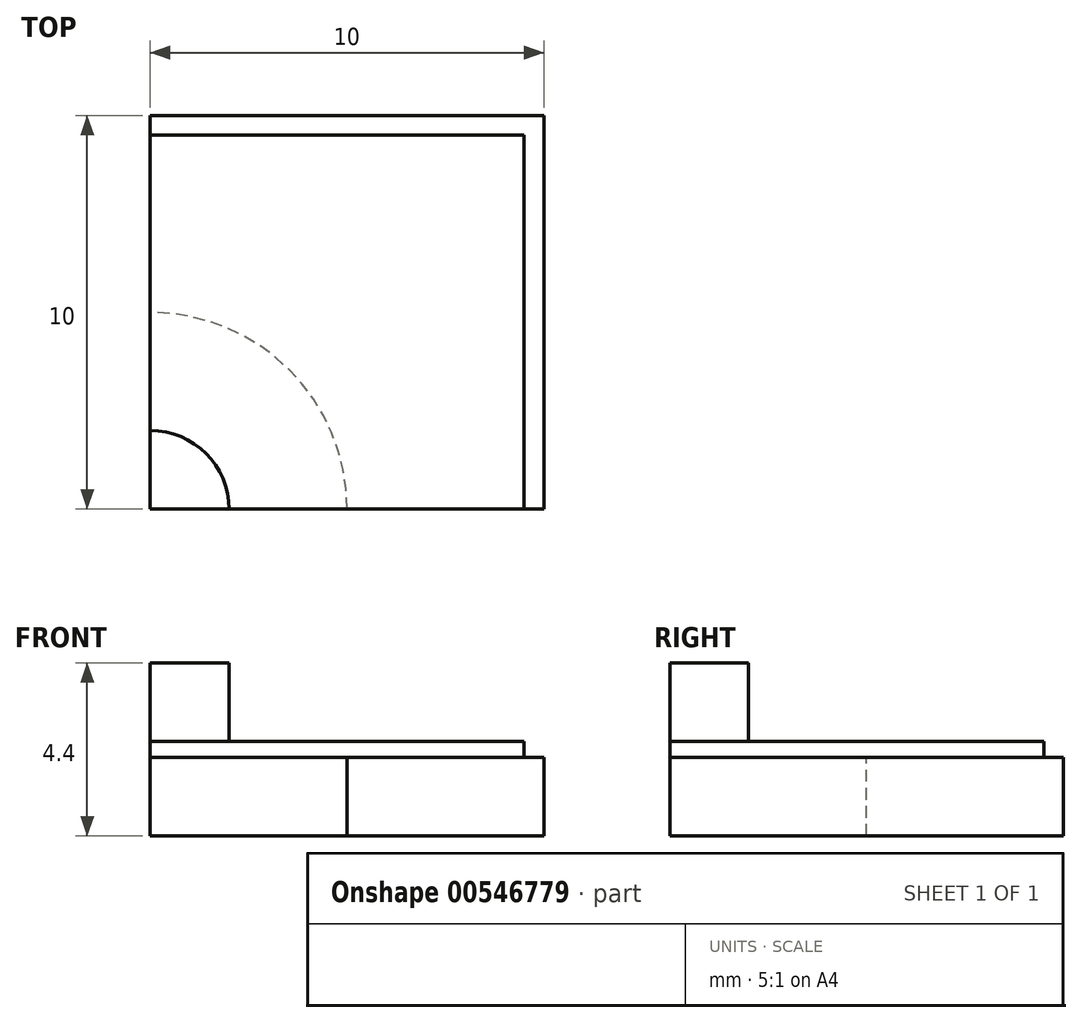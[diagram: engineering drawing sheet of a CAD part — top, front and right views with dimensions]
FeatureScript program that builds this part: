
annotation { "Feature Type Name" : "Feature", "Feature Type Description" : "" }
export const myFeature = defineFeature(function(context is Context, id is Id, definition is map)
    precondition{}
    {
        {
            var Q0;
            Q0=qCreatedBy(makeId("Top.planeOp"),FACE);
            var sketch = newSketch(context, id + "F0", { "sketchPlane" : qUnion([Q0])});
            skLineSegment(sketch, "E0.bottom", {"start": v(0, 0) * mm, "end": v(10, 0) * mm, "construction": true});
            skLineSegment(sketch, "E0.top", {"start": v(0, 10) * mm, "end": v(10, 10) * mm, "construction": true});
            skLineSegment(sketch, "E0.left", {"start": v(0, 0) * mm, "end": v(0, 10) * mm, "construction": true});
            skLineSegment(sketch, "E0.right", {"start": v(10, 0) * mm, "end": v(10, 10) * mm, "construction": true});
            skCircle(sketch, "E1", {"center": v(0, 0) * mm, "radius": 5 * mm, "construction": true});
            skArc(sketch, "E2", {"start": v(5, 0) * mm, "mid": v(3.54, 3.54) * mm, "end": v(0, 5) * mm});
            skLineSegment(sketch, "E3", {"start": v(0, 5) * mm, "end": v(0, 10) * mm});
            skLineSegment(sketch, "E4", {"start": v(10, 10) * mm, "end": v(10, 0) * mm});
            skLineSegment(sketch, "E5", {"start": v(5, 0) * mm, "end": v(10, 0) * mm});
            skLineSegment(sketch, "E6", {"start": v(10, 10) * mm, "end": v(0, 10) * mm});
            skSolve(sketch);
        }
        {
            var Q0;
            Q0=makeQuery(id+"F0.imprint","IMPRINT",FACE,{"disambiguationData":[TD([[makeQuery(id+"F0.imprint","IMPRINT",EDGE,{"derivedFrom":sQuery(id+"F0.wireOp",EDGE,"E2")}),-1.0]])]});
            extrude(context, id + "F1", {"entities" : qUnion([Q0]), "oppositeDirection" : true, "depth" : 2 * mm, "offsetDistance" : 25 * mm});
        }
        {
            var Q0;
            Q0=makeQuery(id+"F1.opExtrude","CAP_FACE",FACE,{"disambiguationData":[OSD([sQuery(id+"F0.wireOp",EDGE,"E2"),sQuery(id+"F0.wireOp",EDGE,"E3"),sQuery(id+"F0.wireOp",EDGE,"E4"),sQuery(id+"F0.wireOp",EDGE,"E5"),sQuery(id+"F0.wireOp",EDGE,"E6")])],"isStart":true});
            var sketch = newSketch(context, id + "F2", { "sketchPlane" : qUnion([Q0])});
            skLineSegment(sketch, "E7.0.0", {"start": v(10, 0) * mm, "end": v(10, 10) * mm, "construction": true});
            skLineSegment(sketch, "E7.0.1", {"start": v(10, 10) * mm, "end": v(0, 10) * mm, "construction": true});
            skLineSegment(sketch, "E7.0.2", {"start": v(0, 10) * mm, "end": v(0, 5) * mm, "construction": true});
            skArc(sketch, "E7.0.3", {"start": v(0, 5) * mm, "mid": v(3.54, 3.54) * mm, "end": v(5, 0) * mm, "construction": true});
            skLineSegment(sketch, "E7.0.4", {"start": v(5, 0) * mm, "end": v(10, 0) * mm, "construction": true});
            skLineSegment(sketch, "E8.bottom", {"start": v(0, 0) * mm, "end": v(9.5, 0) * mm});
            skLineSegment(sketch, "E8.top", {"start": v(0, 9.5) * mm, "end": v(9.5, 9.5) * mm});
            skLineSegment(sketch, "E8.left", {"start": v(0, 0) * mm, "end": v(0, 9.5) * mm});
            skLineSegment(sketch, "E8.right", {"start": v(9.5, 0) * mm, "end": v(9.5, 9.5) * mm});
            skSolve(sketch);
        }
        {
            var Q0;
            {var subQ1=makeQuery(id+"F1.opExtrude","CAP_EDGE",EDGE,{"disambiguationData":[OSD([sQuery(id+"F0.wireOp",EDGE,"E2")])],"isStart":true});Q0=makeQuery(id+"F2.imprint","IMPRINT",FACE,{"disambiguationData":[TD([[makeQuery(id+"F2.imprint","IMPRINT",EDGE,{"derivedFrom":subQ1}),1.0]])]});}
            var Q1;
            {var subQ3=sQuery(id+"F2.wireOp",EDGE,"E8.top");Q1=makeQuery(id+"F2.imprint","IMPRINT",FACE,{"disambiguationData":[TD([[makeQuery(id+"F2.imprint","IMPRINT",EDGE,{"derivedFrom":subQ3}),-1.0]])]});}
            extrude(context, id + "F3", {"entities" : qUnion([Q0, Q1]), "depth" : 0.4 * mm, "offsetDistance" : 25 * mm});
        }
        {
            var Q0;
            Q0=makeQuery(id+"F3.opExtrude","CAP_FACE",FACE,{"disambiguationData":[OSD([sQuery(id+"F2.wireOp",EDGE,"E8.bottom"),sQuery(id+"F2.wireOp",EDGE,"E8.top"),sQuery(id+"F2.wireOp",EDGE,"E8.left"),sQuery(id+"F2.wireOp",EDGE,"E8.right")])],"isStart":false});
            var sketch = newSketch(context, id + "F4", { "sketchPlane" : qUnion([Q0])});
            skArc(sketch, "E9", {"start": v(2, 0) * mm, "mid": v(1.41, 1.41) * mm, "end": v(0, 2) * mm});
            skLineSegment(sketch, "E10", {"start": v(0, 2) * mm, "end": v(0, 0) * mm});
            skLineSegment(sketch, "E11", {"start": v(2, 0) * mm, "end": v(0, 0) * mm});
            skSolve(sketch);
        }
        {
            var Q0;
            Q0=qSketchRegion(id+"F4",true);
            extrude(context, id + "F5", {"entities" : qUnion([Q0]), "depth" : 2 * mm, "offsetDistance" : 25 * mm});
        }
    });
